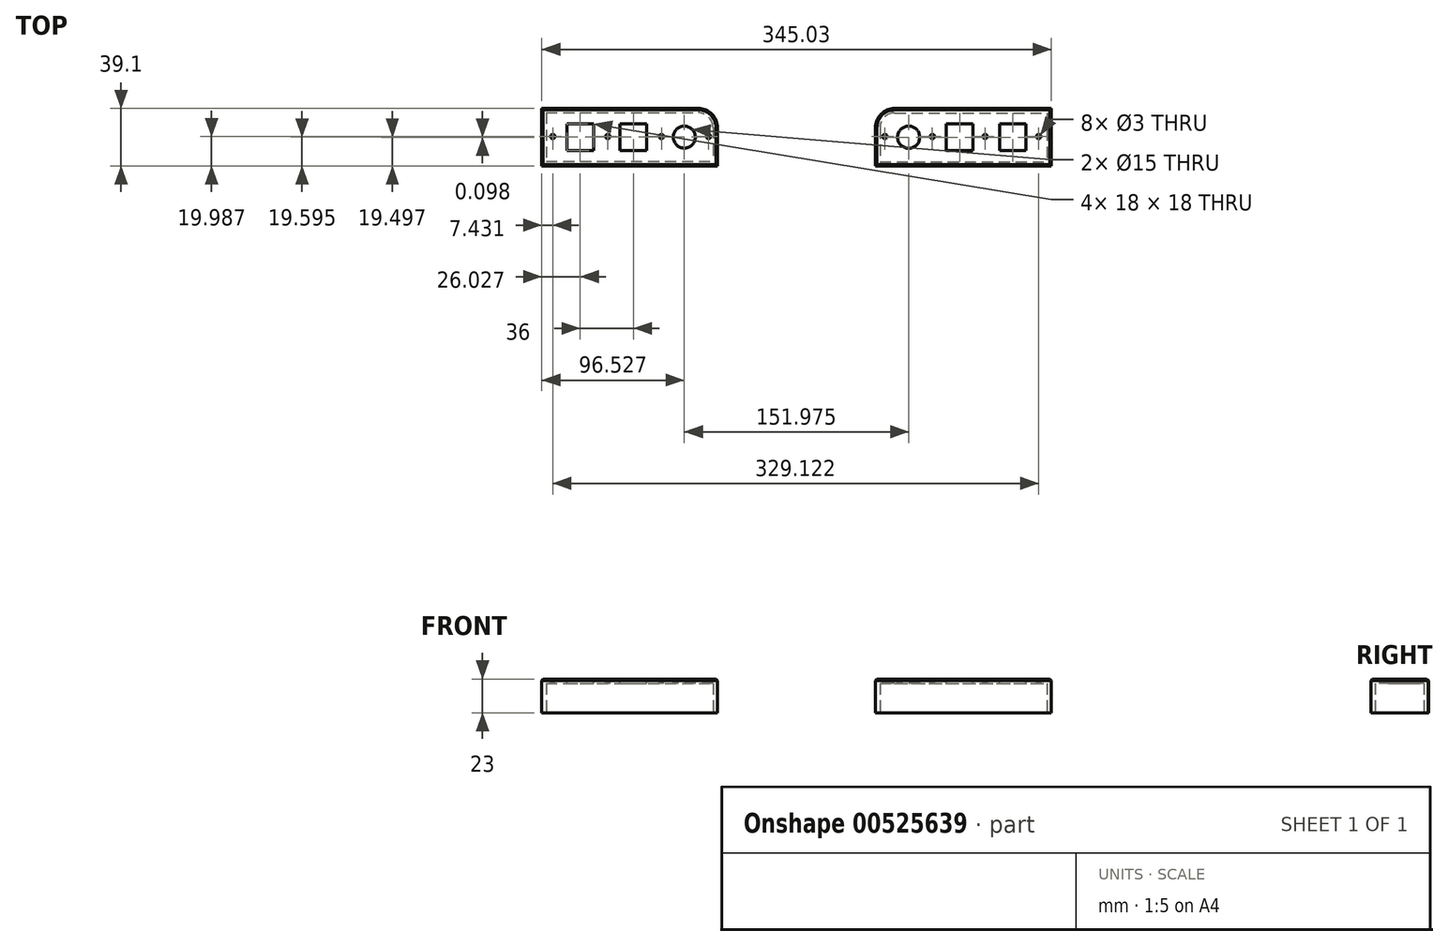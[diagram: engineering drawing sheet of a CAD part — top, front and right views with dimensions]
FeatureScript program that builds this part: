
annotation { "Feature Type Name" : "Feature", "Feature Type Description" : "" }
export const myFeature = defineFeature(function(context is Context, id is Id, definition is map)
    precondition{}
    {
        {
            var Q0;
            Q0=qCreatedBy(makeId("Top.planeOp"),FACE);
            var sketch = newSketch(context, id + "F0", { "sketchPlane" : qUnion([Q0])});
            skLineSegment(sketch, "E0.bottom", {"start": v(66.11, 78.9) * mm, "end": v(169.11, 78.9) * mm});
            skLineSegment(sketch, "E0.top", {"start": v(56.11, 45.9) * mm, "end": v(169.11, 45.9) * mm});
            skLineSegment(sketch, "E0.left", {"start": v(56.11, 68.9) * mm, "end": v(56.11, 45.9) * mm});
            skLineSegment(sketch, "E0.right", {"start": v(169.11, 78.9) * mm, "end": v(169.11, 45.9) * mm});
            skLineSegment(sketch, "E1.bottom", {"start": v(-169.92, 79) * mm, "end": v(-66.92, 79) * mm});
            skLineSegment(sketch, "E1.top", {"start": v(-169.92, 46) * mm, "end": v(-56.92, 46) * mm});
            skLineSegment(sketch, "E1.left", {"start": v(-169.92, 79) * mm, "end": v(-169.92, 46) * mm});
            skLineSegment(sketch, "E1.right", {"start": v(-56.92, 69) * mm, "end": v(-56.92, 46) * mm});
            skPoint(sketch, "E2.visualSharp", {"position": v(-56.92, 79) * mm});
            skArc(sketch, "E2.filletArc", {"start": v(-56.92, 69) * mm, "mid": v(-59.85, 76.07) * mm, "end": v(-66.92, 79) * mm});
            skPoint(sketch, "E3.visualSharp", {"position": v(56.11, 78.9) * mm});
            skArc(sketch, "E3.filletArc", {"start": v(66.11, 78.9) * mm, "mid": v(59.04, 75.97) * mm, "end": v(56.11, 68.9) * mm});
            skSolve(sketch);
        }
        {
            var Q0;
            Q0=qSketchRegion(id+"F0",true);
            extrude(context, id + "F1", {"entities" : qUnion([Q0]), "depth" : 5 * mm, "hasSecondDirection" : true, "secondDirectionOppositeDirection" : true, "secondDirectionDepth" : 15 * mm, "offsetDistance" : 25 * mm});
        }
        {
            var Q0;
            Q0=makeQuery(id+"F1.opExtrude","CAP_FACE",FACE,{"disambiguationData":[OSD([sQuery(id+"F0.wireOp",EDGE,"E0.bottom"),sQuery(id+"F0.wireOp",EDGE,"E0.top"),sQuery(id+"F0.wireOp",EDGE,"E0.left"),sQuery(id+"F0.wireOp",EDGE,"E0.right"),sQuery(id+"F0.wireOp",EDGE,"E3.filletArc")])],"isStart":true});
            var Q1;
            Q1=makeQuery(id+"F1.opExtrude","CAP_FACE",FACE,{"disambiguationData":[OSD([sQuery(id+"F0.wireOp",EDGE,"E1.bottom"),sQuery(id+"F0.wireOp",EDGE,"E1.top"),sQuery(id+"F0.wireOp",EDGE,"E1.left"),sQuery(id+"F0.wireOp",EDGE,"E1.right"),sQuery(id+"F0.wireOp",EDGE,"E2.filletArc")])],"isStart":true});
            shell(context, id + "F2", {"entities" : qUnion([Q0, Q1]), "thickness" : 3 * mm, "oppositeDirection" : true});
        }
        {
            var Q0;
            Q0=makeQuery(id+"F1.opExtrude","CAP_FACE",FACE,{"disambiguationData":[OSD([sQuery(id+"F0.wireOp",EDGE,"E0.bottom"),sQuery(id+"F0.wireOp",EDGE,"E0.top"),sQuery(id+"F0.wireOp",EDGE,"E0.left"),sQuery(id+"F0.wireOp",EDGE,"E0.right"),sQuery(id+"F0.wireOp",EDGE,"E3.filletArc")])],"isStart":false});
            cPlane(context, id + "F3", {"entities" : qUnion([Q0]), "cplaneType" : CPlaneType.OFFSET, "offset" : 25 * mm, "width" : 150 * mm, "height" : 150 * mm});
        }
        {
            var Q0;
            Q0=qCreatedBy(id+"F3.planeOp",FACE);
            var sketch = newSketch(context, id + "F4", { "sketchPlane" : qUnion([Q0])});
            skLineSegment(sketch, "E4.bottom", {"start": v(-155.9, 71.5) * mm, "end": v(-137.9, 71.5) * mm});
            skLineSegment(sketch, "E4.top", {"start": v(-155.9, 53.5) * mm, "end": v(-137.9, 53.5) * mm});
            skLineSegment(sketch, "E4.left", {"start": v(-155.9, 71.5) * mm, "end": v(-155.9, 53.5) * mm});
            skLineSegment(sketch, "E4.right", {"start": v(-137.9, 71.5) * mm, "end": v(-137.9, 53.5) * mm});
            skLineSegment(sketch, "E5.bottom", {"start": v(-119.9, 71.5) * mm, "end": v(-101.9, 71.5) * mm});
            skLineSegment(sketch, "E5.top", {"start": v(-119.9, 53.5) * mm, "end": v(-101.9, 53.5) * mm});
            skLineSegment(sketch, "E5.left", {"start": v(-119.9, 71.5) * mm, "end": v(-119.9, 53.5) * mm});
            skLineSegment(sketch, "E5.right", {"start": v(-101.9, 71.5) * mm, "end": v(-101.9, 53.5) * mm});
            skCircle(sketch, "E6", {"center": v(-76.4, 62.5) * mm, "radius": 7.5 * mm});
            skCircle(sketch, "E7", {"center": v(75.58, 62.4) * mm, "radius": 7.5 * mm});
            skLineSegment(sketch, "E8.bottom", {"start": v(101.08, 71.4) * mm, "end": v(119.08, 71.4) * mm});
            skLineSegment(sketch, "E8.top", {"start": v(101.08, 53.4) * mm, "end": v(119.08, 53.4) * mm});
            skLineSegment(sketch, "E8.left", {"start": v(101.08, 71.4) * mm, "end": v(101.08, 53.4) * mm});
            skLineSegment(sketch, "E8.right", {"start": v(119.08, 71.4) * mm, "end": v(119.08, 53.4) * mm});
            skLineSegment(sketch, "E9.bottom", {"start": v(137.08, 71.4) * mm, "end": v(155.08, 71.4) * mm});
            skLineSegment(sketch, "E9.top", {"start": v(137.08, 53.4) * mm, "end": v(155.08, 53.4) * mm});
            skLineSegment(sketch, "E9.left", {"start": v(137.08, 71.4) * mm, "end": v(137.08, 53.4) * mm});
            skLineSegment(sketch, "E9.right", {"start": v(155.08, 71.4) * mm, "end": v(155.08, 53.4) * mm});
            skSolve(sketch);
        }
        {
            var Q0;
            Q0=qSketchRegion(id+"F4",true);
            extrude(context, id + "F5", {"entities" : qUnion([Q0]), "operationType" : NewBodyOperationType.REMOVE, "oppositeDirection" : true, "depth" : 50 * mm});
        }
        {
            var Q0;
            Q0=makeQuery(id+"F1.opExtrude","CAP_FACE",FACE,{"disambiguationData":[OSD([sQuery(id+"F0.wireOp",EDGE,"E1.bottom"),sQuery(id+"F0.wireOp",EDGE,"E1.top"),sQuery(id+"F0.wireOp",EDGE,"E1.left"),sQuery(id+"F0.wireOp",EDGE,"E1.right"),sQuery(id+"F0.wireOp",EDGE,"E2.filletArc")])],"isStart":false});
            cPlane(context, id + "F6", {"entities" : qUnion([Q0]), "cplaneType" : CPlaneType.OFFSET, "offset" : 0 * mm, "width" : 150 * mm, "height" : 150 * mm});
        }
        {
            var Q0;
            Q0=qCreatedBy(id+"F6.planeOp",FACE);
            var sketch = newSketch(context, id + "F7", { "sketchPlane" : qUnion([Q0])});
            skPoint(sketch, "E10", {"position": v(-165.49, 62.89) * mm});
            skPoint(sketch, "E11", {"position": v(-128.13, 62.89) * mm});
            skPoint(sketch, "E12", {"position": v(-91.87, 62.89) * mm});
            skPoint(sketch, "E13", {"position": v(-59.97, 62.89) * mm});
            skPoint(sketch, "E14", {"position": v(59.47, 62.89) * mm});
            skPoint(sketch, "E15", {"position": v(91.64, 62.89) * mm});
            skPoint(sketch, "E16", {"position": v(127.36, 62.89) * mm});
            skPoint(sketch, "E17", {"position": v(163.63, 62.89) * mm});
            skSolve(sketch);
        }
        {
            var Q0;
            Q0=sQuery(id+"F7.wireOp",VERTEX,"E11");
            var Q1;
            Q1=sQuery(id+"F7.wireOp",VERTEX,"E17");
            var Q2;
            Q2=sQuery(id+"F7.wireOp",VERTEX,"E16");
            var Q3;
            Q3=sQuery(id+"F7.wireOp",VERTEX,"E10");
            var Q4;
            Q4=sQuery(id+"F7.wireOp",VERTEX,"E15");
            var Q5;
            Q5=sQuery(id+"F7.wireOp",VERTEX,"E14");
            var Q6;
            Q6=sQuery(id+"F7.wireOp",VERTEX,"E12");
            var Q7;
            Q7=sQuery(id+"F7.wireOp",VERTEX,"E13");
            var Q8;
            Q8=makeQuery(id+"F1.opExtrude","SWEPT_BODY",BODY,{"disambiguationData":[OSD([sQuery(id+"F0.wireOp",EDGE,"E0.bottom"),sQuery(id+"F0.wireOp",EDGE,"E0.top"),sQuery(id+"F0.wireOp",EDGE,"E0.left"),sQuery(id+"F0.wireOp",EDGE,"E0.right"),sQuery(id+"F0.wireOp",EDGE,"E3.filletArc")])]});
            var Q9;
            Q9=makeQuery(id+"F1.opExtrude","SWEPT_BODY",BODY,{"disambiguationData":[OSD([sQuery(id+"F0.wireOp",EDGE,"E1.bottom"),sQuery(id+"F0.wireOp",EDGE,"E1.top"),sQuery(id+"F0.wireOp",EDGE,"E1.left"),sQuery(id+"F0.wireOp",EDGE,"E1.right"),sQuery(id+"F0.wireOp",EDGE,"E2.filletArc")])]});
            hole(context, id + "F8", {"style" : HoleStyle.SIMPLE, "endStyle" : HoleEndStyle.BLIND, "holeDiameter" : 3 * mm, "holeDepth" : 40 * mm, "startFromSketch" : true, "locations" : qUnion([Q0, Q1, Q2, Q3, Q4, Q5, Q6, Q7]), "scope" : qUnion([Q8, Q9])});
        }
        {
            var Q0;
            Q0=makeQuery(id+"F1.opExtrude","CAP_EDGE",EDGE,{"disambiguationData":[OSD([sQuery(id+"F0.wireOp",EDGE,"E1.top")])],"isStart":false});
            var Q1;
            Q1=makeQuery(id+"F1.opExtrude","CAP_EDGE",EDGE,{"disambiguationData":[OSD([sQuery(id+"F0.wireOp",EDGE,"E1.left")])],"isStart":false});
            var Q2;
            Q2=makeQuery(id+"F1.opExtrude","CAP_EDGE",EDGE,{"disambiguationData":[OSD([sQuery(id+"F0.wireOp",EDGE,"E1.bottom")])],"isStart":false});
            var Q3;
            Q3=makeQuery(id+"F1.opExtrude","CAP_EDGE",EDGE,{"disambiguationData":[OSD([sQuery(id+"F0.wireOp",EDGE,"E0.left")])],"isStart":false});
            var Q4;
            Q4=makeQuery(id+"F1.opExtrude","CAP_EDGE",EDGE,{"disambiguationData":[OSD([sQuery(id+"F0.wireOp",EDGE,"E0.top")])],"isStart":false});
            var Q5;
            Q5=makeQuery(id+"F1.opExtrude","CAP_EDGE",EDGE,{"disambiguationData":[OSD([sQuery(id+"F0.wireOp",EDGE,"E0.right")])],"isStart":false});
            chamfer(context, id + "F9", {"entities" : qUnion([Q0, Q1, Q2, Q3, Q4, Q5]), "width" : 1 * mm, "tangentPropagation" : true});
        }
    });
